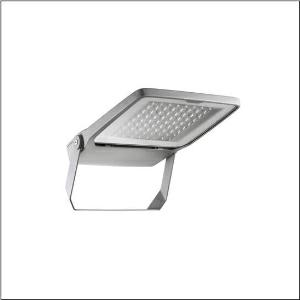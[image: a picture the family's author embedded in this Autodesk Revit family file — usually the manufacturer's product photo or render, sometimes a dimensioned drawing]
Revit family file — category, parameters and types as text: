
# Revit family: floodlight_fl_20_mini___pl52_5xa7671b2d1ac_96f2
name_source: partatom
category: Lighting Fixtures
units: mm (PartAtom-declared; Revit-internal decimal feet)

## family parameters
Cut with Voids When Loaded = No
Host = Face
Light Source = No
Part Type = Normal
Room Calculation Point = No
Round Connector Dimension = Use Diameter
Shared = No

## types (1)
- Floodlight FL 20 mini  PL52 (1 x LED 4000K / CRI = 70 (unbekannt), 6270 lm, 4000K)
    Apparent Load = 51 VA
    CIE Flux Codes = 27 59 98 100 100
    Color Rendering = 70
    Color Temperature = 4000K
    Default Elevation = 1800 mm
    Description = Floodlight FL 20 mini, floodlight, primary light control with lens, of plastic, primary optical cover: protective disc, of toughened safety glass, transparent, light distribution: PL52, light emission: direct distribution, primary light characteristic: asymmetric, installation type: surface-mounted, LED, High Power LED, rated luminous flux: 6.270lm, luminous efficacy: 123lm/W, light colour: 740, colour temperature: 4000K, control gear: ECG Basic, control: overheat protection, power reduction, electronic power reduction, with terminal, 5-pole, max. 2.5mm², mains connection: 220..240V, AC, 50/60Hz, rated input power: 51W, LED unit, of diecast aluminium, powder-coated, Siteco® metallic grey (DB 702S), corrosivity category C5 mid according to DIN EN ISO 12944, incl. 1x M20 cable gland for cable Ø 6.5..12mm, length: 446mm, width: 355mm, height: 62mm, housing frame, of diecast aluminium, powder-coated, Siteco® metallic grey (DB 702S), mounting bracket, of steel, powder-coated, Siteco® metallic grey (DB 702S), ON/OFF, protection rating (complete): IP66, insulation class (complete): insulation class I (protective earthing), certification: CE, ENEC, VDE, protection symbol: D, permissible operating ambient temperature: -40..+40°C, permissible operating ambient temperature for outdoor applications: -40..+50°C, standard: DIN EN 12944, packaging unit: 1 piece

Light Distribution: PL52
    Height = 62 mm  [stored 0.203412 ft]
    Lamp = 1 x LED 4000K / CRI >= 70 (unbekannt)
    Lamp Light Flux = 6270 lm
    Lamp count = 1
    Length = 467 mm
    Luminous efficacy = 123 lm/W
    Manufacturer = Siteco
    ModVariant = No
    Model = 5XA7671B2D1AC
    Mounting Place = Wall
    Mounting Type = Surface mounted
    Number of Poles = 1
    OnlyDefault = Yes
    Power Factor = 1
    Product Name = Floodlight FL 20 mini | PL52
    Product group = floodlight | wall mounted
    ProductGroupID = 2001
    Protection Class = Protection class I
    Protection Degree = IP 66
    RLX_Detail_Level = 1
    RLX_Emergency_Light_Flux = 0 lm
    RLX_Emergency_Type = 0
    RLX_Emergency_Type_DB = No
    RlxData = <blob elided: 71025 chars, md5=0ed47843>
    Socket = socket
    Standby Power = 0 W
    System Light Flux = 6270 lm
    System Power = 51 W
    Type Comments = Product without accessories
    Type Image = l_1005948.jpg
    URL = http://relux.com
    VarID = ---
    Voltage = 0 V
    Weight = 0.00 kg
    Width = 335 mm

note: [stored X ft] marks values corroborated as IEEE doubles in the binary element streams (Revit-internal decimal feet)

## geometry (parser evidence)
native form markers: Blend x4, Sweep x12
no freeform markers — native parametric forms only
